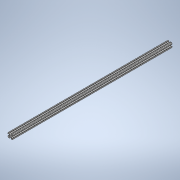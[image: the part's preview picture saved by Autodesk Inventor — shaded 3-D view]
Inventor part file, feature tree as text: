
AUTODESK INVENTOR PART (.ipt)
format: ipt  version: 2020 (Build 240168000, 168)  size: 244,736 bytes
history: native  units: in
note: dims shown in document units (in); Inventor stores cm internally (conversion verified against a paired STEP export)
features: extrude x1, sketch x1
ambient origin geometry x8: Origin, YZ Plane, XZ Plane, XY Plane, X Axis, Y Axis, Z Axis, Center Point
bodies: Solid1 (feature_tree)
feature tree (2):
  extrude  "Extrusion1"  Depth=34.0in
  sketch  "Sketch1"  dims[d0=34.0in d1=0.0in d2=0.5in d3=0.0344in d4=0.5in d5=0.0344in]
